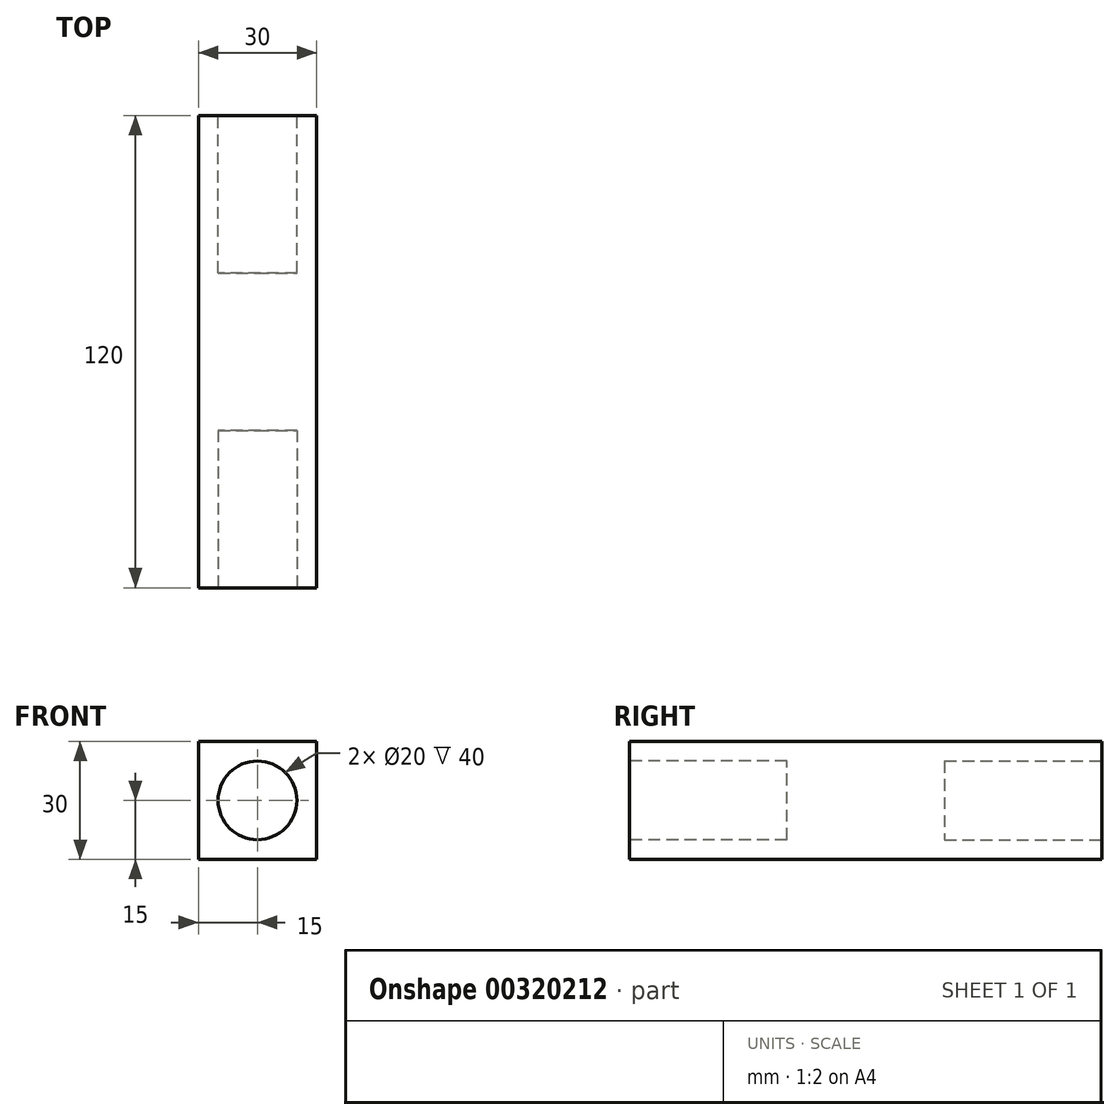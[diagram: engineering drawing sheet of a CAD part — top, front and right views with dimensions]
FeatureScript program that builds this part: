
annotation { "Feature Type Name" : "Feature", "Feature Type Description" : "" }
export const myFeature = defineFeature(function(context is Context, id is Id, definition is map)
    precondition{}
    {
        {
            var Q0;
            Q0=qCreatedBy(makeId("Front.planeOp"),FACE);
            var sketch = newSketch(context, id + "F0", { "sketchPlane" : qUnion([Q0])});
            skPoint(sketch, "E0.orphan", {"position": v(-15, 0) * mm});
            skLineSegment(sketch, "E1", {"start": v(15, 0) * mm, "end": v(15, 15) * mm});
            skLineSegment(sketch, "E2", {"start": v(15, 15) * mm, "end": v(0, 15) * mm});
            skLineSegment(sketch, "E3", {"start": v(-15, 15) * mm, "end": v(-15, -15) * mm});
            skLineSegment(sketch, "E4", {"start": v(-15, -15) * mm, "end": v(15, -15) * mm});
            skLineSegment(sketch, "E5", {"start": v(15, -15) * mm, "end": v(15, 0) * mm});
            skLineSegment(sketch, "E6", {"start": v(-15, 15) * mm, "end": v(0, 15) * mm});
            skSolve(sketch);
        }
        {
            var Q0;
            Q0=qSketchRegion(id+"F0",true);
            extrude(context, id + "F1", {"entities" : qUnion([Q0]), "endBound" : BoundingType.SYMMETRIC, "depth" : 120 * mm});
        }
        {
            var Q0;
            Q0=makeQuery(id+"F1.opExtrude","CAP_FACE",FACE,{"disambiguationData":[OSD([sQuery(id+"F0.wireOp",EDGE,"E1"),sQuery(id+"F0.wireOp",EDGE,"E2"),sQuery(id+"F0.wireOp",EDGE,"E3"),sQuery(id+"F0.wireOp",EDGE,"E4"),sQuery(id+"F0.wireOp",EDGE,"E5"),sQuery(id+"F0.wireOp",EDGE,"E6")])],"isStart":false});
            var sketch = newSketch(context, id + "F2", { "sketchPlane" : qUnion([Q0])});
            skCircle(sketch, "E7", {"center": v(0, 0) * mm, "radius": 10 * mm});
            skSolve(sketch);
        }
        {
            var Q0;
            Q0=qSketchRegion(id+"F2",true);
            extrude(context, id + "F3", {"entities" : qUnion([Q0]), "operationType" : NewBodyOperationType.REMOVE, "oppositeDirection" : true, "depth" : 40 * mm});
        }
        {
            var Q0;
            Q0=makeQuery(id+"F1.opExtrude","CAP_FACE",FACE,{"disambiguationData":[OSD([sQuery(id+"F0.wireOp",EDGE,"E1"),sQuery(id+"F0.wireOp",EDGE,"E2"),sQuery(id+"F0.wireOp",EDGE,"E3"),sQuery(id+"F0.wireOp",EDGE,"E4"),sQuery(id+"F0.wireOp",EDGE,"E5"),sQuery(id+"F0.wireOp",EDGE,"E6")])],"isStart":true});
            var sketch = newSketch(context, id + "F4", { "sketchPlane" : qUnion([Q0])});
            skCircle(sketch, "E8", {"center": v(0, 0) * mm, "radius": 10 * mm});
            skSolve(sketch);
        }
        {
            var Q0;
            Q0=qSketchRegion(id+"F4",true);
            extrude(context, id + "F5", {"entities" : qUnion([Q0]), "operationType" : NewBodyOperationType.REMOVE, "oppositeDirection" : true, "depth" : 40 * mm});
        }
    });
